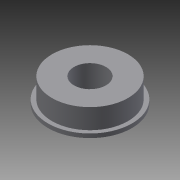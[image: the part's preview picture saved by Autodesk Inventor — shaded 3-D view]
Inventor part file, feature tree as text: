
AUTODESK INVENTOR PART (.ipt)
format: ipt  version: 2013 (Build 170138000, 138)  size: 87,552 bytes
history: native  units: in
note: dims shown in document units (in); Inventor stores cm internally (conversion verified against a paired STEP export)
features: extrude x2, sketch x2
ambient origin geometry x8: Origin, YZ Plane, XZ Plane, XY Plane, X Axis, Y Axis, Z Axis, Center Point
bodies: Solid1 (feature_tree)
feature tree (4):
  extrude  "Extrusion1"  Depth=0.315in
  extrude  "Extrusion2"  Depth=0.748in
  sketch  "Sketch1"  dims[d0=0.8268in d1=0.315in]
  sketch  "Sketch2"  dims[d2=0.0394in d3=0.0in d4=0.748in d5=0.1969in d6=0.0in]
